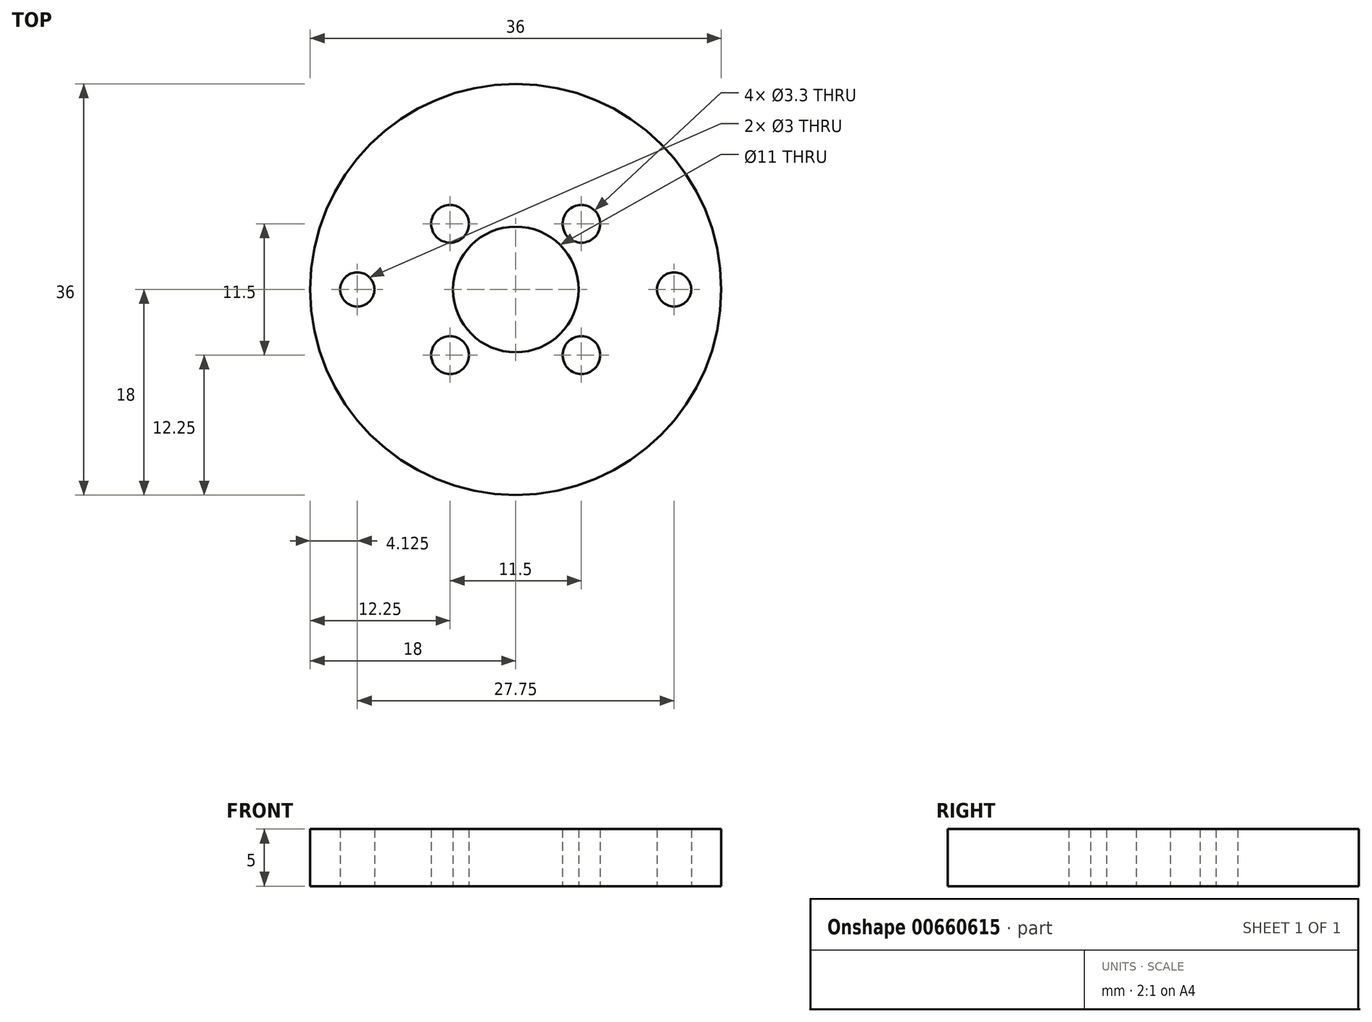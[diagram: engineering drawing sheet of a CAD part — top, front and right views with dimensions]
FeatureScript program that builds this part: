
annotation { "Feature Type Name" : "Feature", "Feature Type Description" : "" }
export const myFeature = defineFeature(function(context is Context, id is Id, definition is map)
    precondition{}
    {
        {
            var Q0;
            Q0=qCreatedBy(makeId("Top.planeOp"),FACE);
            var sketch = newSketch(context, id + "F0", { "sketchPlane" : qUnion([Q0])});
            skCircle(sketch, "E0", {"center": v(0, 0) * mm, "radius": 18 * mm});
            skLineSegment(sketch, "E1.bottom", {"start": v(5.75, 5.75) * mm, "end": v(-5.75, 5.75) * mm, "construction": true});
            skLineSegment(sketch, "E1.top", {"start": v(5.75, -5.75) * mm, "end": v(-5.75, -5.75) * mm, "construction": true});
            skLineSegment(sketch, "E1.left", {"start": v(5.75, 5.75) * mm, "end": v(5.75, -5.75) * mm, "construction": true});
            skLineSegment(sketch, "E1.right", {"start": v(-5.75, 5.75) * mm, "end": v(-5.75, -5.75) * mm, "construction": true});
            skCircle(sketch, "E2", {"center": v(0, 0) * mm, "radius": 9.75 * mm});
            skLineSegment(sketch, "E3", {"start": v(-18, 0) * mm, "end": v(-9.75, 0) * mm});
            skLineSegment(sketch, "E4", {"start": v(9.75, 0) * mm, "end": v(18, 0) * mm});
            skPoint(sketch, "E4.startSnap0", {"position": v(5.75, 0) * mm});
            skPoint(sketch, "E5", {"position": v(-13.88, 0) * mm});
            skPoint(sketch, "E6", {"position": v(13.87, 0) * mm});
            skSolve(sketch);
        }
        {
            var Q0;
            {var subQ0=sQuery(id+"F0.wireOp",EDGE,"E3");Q0=makeQuery(id+"F0.imprint","IMPRINT",FACE,{"disambiguationData":[TD([[makeQuery(id+"F0.imprint","IMPRINT",EDGE,{"derivedFrom":subQ0}),1.0]])]});}
            var Q1;
            {var subQ0=sQuery(id+"F0.wireOp",EDGE,"E3");Q1=makeQuery(id+"F0.imprint","IMPRINT",FACE,{"disambiguationData":[TD([[makeQuery(id+"F0.imprint","IMPRINT",EDGE,{"derivedFrom":subQ0}),-1.0]])]});}
            var Q2;
            {var subQ0=sQuery(id+"F0.wireOp",EDGE,"E2");var subQ1=makeQuery(id+"F0.imprint","INTERSECT",VERTEX,{"derivedFrom":[subQ0,sQuery(id+"F0.wireOp",EDGE,"E3")]});Q2=makeQuery(id+"F0.imprint","IMPRINT",FACE,{"disambiguationData":[TD([[makeQuery(id+"F0.imprint","IMPRINT",EDGE,{"disambiguationData":[TD([[subQ1,1.0]])],"derivedFrom":subQ0}),1.0]])]});}
            extrude(context, id + "F1", {"entities" : qUnion([Q0, Q1, Q2]), "depth" : 5 * mm, "offsetDistance" : 25 * mm});
        }
        {
            var Q0;
            Q0=sQuery(id+"F0.wireOp",VERTEX,"E6");
            var Q1;
            Q1=sQuery(id+"F0.wireOp",VERTEX,"E5");
            var Q2;
            Q2=makeQuery(id+"F1.opExtrude","SWEPT_BODY",BODY,{"disambiguationData":[OSD([sQuery(id+"F0.wireOp",EDGE,"E0")])]});
            hole(context, id + "F2", {"style" : HoleStyle.SIMPLE, "endStyle" : HoleEndStyle.BLIND, "oppositeDirection" : true, "holeDiameter" : 3 * mm, "majorDiameter" : 5 * mm, "holeDepth" : 6 * mm, "isTappedThrough" : true, "tappedDepth" : 12 * mm, "tapClearance" : 3, "locations" : qUnion([Q0, Q1]), "scope" : qUnion([Q2])});
        }
        {
            var Q0;
            Q0=sQuery(id+"F0.wireOp",VERTEX,"E1.bottom.start");
            var Q1;
            Q1=sQuery(id+"F0.wireOp",VERTEX,"E1.left.end");
            var Q2;
            Q2=sQuery(id+"F0.wireOp",VERTEX,"E1.right.end");
            var Q3;
            Q3=sQuery(id+"F0.wireOp",VERTEX,"E1.right.start");
            var Q4;
            Q4=makeQuery(id+"F1.opExtrude","SWEPT_BODY",BODY,{"disambiguationData":[OSD([sQuery(id+"F0.wireOp",EDGE,"E0")])]});
            hole(context, id + "F3", {"style" : HoleStyle.SIMPLE, "endStyle" : HoleEndStyle.BLIND, "oppositeDirection" : true, "standardTappedOrClearance" : lookupTablePath({ "standard" : "ISO", "fit" : "Normal", "size" : "M3", "type" : "Clearance" }), "standardBlindInLast" : lookupTablePath({ "fit" : "Standard", "standard" : "ISO", "size" : "M3", "type" : "Clearance" }), "holeDiameter" : 3.3 * mm, "majorDiameter" : 5 * mm, "holeDepth" : 6 * mm, "isTappedThrough" : true, "tappedDepth" : 12 * mm, "tapClearance" : 3, "locations" : qUnion([Q0, Q1, Q2, Q3]), "scope" : qUnion([Q4])});
        }
        {
            var Q0;
            Q0=sQuery(id+"F0.wireOp",VERTEX,"E0.center");
            var Q1;
            Q1=makeQuery(id+"F1.opExtrude","SWEPT_BODY",BODY,{"disambiguationData":[OSD([sQuery(id+"F0.wireOp",EDGE,"E0")])]});
            hole(context, id + "F4", {"style" : HoleStyle.SIMPLE, "endStyle" : HoleEndStyle.BLIND, "oppositeDirection" : true, "holeDiameter" : 11 * mm, "majorDiameter" : 5 * mm, "holeDepth" : 11 * mm, "isTappedThrough" : true, "tappedDepth" : 12 * mm, "tapClearance" : 3, "locations" : qUnion([Q0]), "scope" : qUnion([Q1])});
        }
    });
